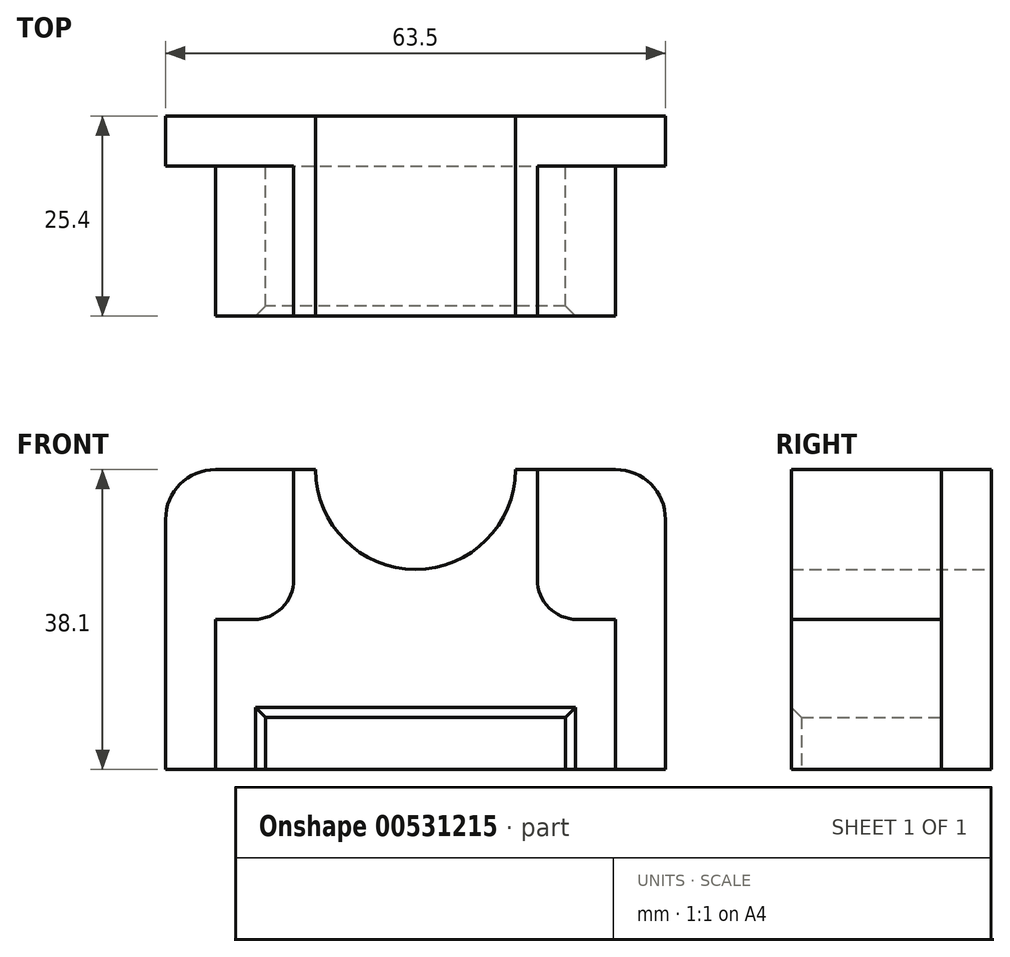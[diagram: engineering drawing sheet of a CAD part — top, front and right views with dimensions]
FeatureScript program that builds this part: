
annotation { "Feature Type Name" : "Feature", "Feature Type Description" : "" }
export const myFeature = defineFeature(function(context is Context, id is Id, definition is map)
    precondition{}
    {
        {
            var Q0;
            Q0=qCreatedBy(makeId("Front.planeOp"),FACE);
            var sketch = newSketch(context, id + "F0", { "sketchPlane" : qUnion([Q0])});
            skLineSegment(sketch, "E0.bottom", {"start": v(-25.4, 19.05) * mm, "end": v(-12.7, 19.05) * mm});
            skLineSegment(sketch, "E0.top", {"start": v(-31.75, -19.05) * mm, "end": v(31.75, -19.05) * mm});
            skLineSegment(sketch, "E0.left", {"start": v(-31.75, 12.7) * mm, "end": v(-31.75, -19.05) * mm});
            skLineSegment(sketch, "E0.right", {"start": v(31.75, 12.7) * mm, "end": v(31.75, -19.05) * mm});
            skPoint(sketch, "E0.middle", {"position": v(0, 0) * mm});
            skPoint(sketch, "E1.visualSharp", {"position": v(31.75, 19.05) * mm});
            skArc(sketch, "E1.filletArc", {"start": v(31.75, 12.7) * mm, "mid": v(29.9, 17.2) * mm, "end": v(25.4, 19.05) * mm});
            skPoint(sketch, "E2.visualSharp", {"position": v(-31.75, 19.05) * mm});
            skArc(sketch, "E2.filletArc", {"start": v(-25.4, 19.05) * mm, "mid": v(-29.9, 17.2) * mm, "end": v(-31.75, 12.7) * mm});
            skArc(sketch, "E3", {"start": v(-12.7, 19.05) * mm, "mid": v(0, 6.35) * mm, "end": v(12.7, 19.05) * mm});
            skLineSegment(sketch, "E4.trimOffspring", {"start": v(12.7, 19.05) * mm, "end": v(25.4, 19.05) * mm});
            skSolve(sketch);
        }
        {
            var Q0;
            Q0=makeQuery(id+"F0.imprint","IMPRINT",FACE,{"disambiguationData":[TD([[makeQuery(id+"F0.imprint","IMPRINT",EDGE,{"derivedFrom":sQuery(id+"F0.wireOp",EDGE,"E0.bottom")}),-1.0]])]});
            extrude(context, id + "F1", {"entities" : qUnion([Q0]), "depth" : 6.35 * mm, "offsetDistance" : 25.4 * mm});
        }
        {
            var Q0;
            Q0=makeQuery(id+"F1.opExtrude","CAP_FACE",FACE,{"disambiguationData":[OSD([sQuery(id+"F0.wireOp",EDGE,"E0.bottom"),sQuery(id+"F0.wireOp",EDGE,"E0.top"),sQuery(id+"F0.wireOp",EDGE,"E0.left"),sQuery(id+"F0.wireOp",EDGE,"E0.right"),sQuery(id+"F0.wireOp",EDGE,"E1.filletArc"),sQuery(id+"F0.wireOp",EDGE,"E2.filletArc"),sQuery(id+"F0.wireOp",EDGE,"E3"),sQuery(id+"F0.wireOp",EDGE,"E4.trimOffspring")])],"isStart":false});
            var sketch = newSketch(context, id + "F2", { "sketchPlane" : qUnion([Q0])});
            skLineSegment(sketch, "E5", {"start": v(-12.7, 19.05) * mm, "end": v(-15.47, 19.05) * mm});
            skLineSegment(sketch, "E6", {"start": v(-19.05, -19.05) * mm, "end": v(-25.4, -19.05) * mm});
            skLineSegment(sketch, "E7", {"start": v(19.05, -19.05) * mm, "end": v(25.4, -19.05) * mm});
            skLineSegment(sketch, "E8", {"start": v(-25.4, -19.05) * mm, "end": v(-25.4, 0) * mm});
            skLineSegment(sketch, "E9", {"start": v(25.4, -19.05) * mm, "end": v(25.4, 0) * mm});
            skLineSegment(sketch, "E10", {"start": v(25.4, -19.05) * mm, "end": v(19.05, -19.05) * mm});
            skLineSegment(sketch, "E11", {"start": v(-25.4, -19.05) * mm, "end": v(-19.05, -19.05) * mm});
            skArc(sketch, "E12", {"start": v(-12.7, 19.05) * mm, "mid": v(0, 6.35) * mm, "end": v(12.7, 19.05) * mm});
            skLineSegment(sketch, "E13", {"start": v(-15.47, 19.05) * mm, "end": v(-15.47, 0) * mm});
            skLineSegment(sketch, "E14", {"start": v(-15.47, 0) * mm, "end": v(-25.4, 0) * mm});
            skLineSegment(sketch, "E15", {"start": v(12.7, 19.05) * mm, "end": v(15.47, 19.05) * mm});
            skLineSegment(sketch, "E16", {"start": v(15.47, 19.05) * mm, "end": v(15.47, 0) * mm});
            skLineSegment(sketch, "E17", {"start": v(15.47, 0) * mm, "end": v(25.4, 0) * mm});
            skLineSegment(sketch, "E18", {"start": v(-19.05, -19.05) * mm, "end": v(-19.05, -12.42) * mm});
            skLineSegment(sketch, "E19", {"start": v(-19.05, -12.42) * mm, "end": v(19.05, -12.42) * mm});
            skLineSegment(sketch, "E20", {"start": v(19.05, -19.05) * mm, "end": v(19.05, -12.42) * mm});
            skPoint(sketch, "E21.orphan", {"position": v(0, -19.05) * mm});
            skSolve(sketch);
        }
        {
            var Q0;
            Q0=makeQuery(id+"F2.imprint","IMPRINT",FACE,{"disambiguationData":[TD([[makeQuery(id+"F2.imprint","IMPRINT",EDGE,{"derivedFrom":sQuery(id+"F2.wireOp",EDGE,"E5")}),-1.0]])]});
            extrude(context, id + "F3", {"entities" : qUnion([Q0]), "operationType" : NewBodyOperationType.ADD, "depth" : 19.05 * mm, "offsetDistance" : 25.4 * mm});
        }
        {
            var Q0;
            Q0=makeQuery(id+"F3.opExtrude","SWEPT_EDGE",EDGE,{"disambiguationData":[OSD([sQuery(id+"F2.wireOp",EDGE,"E13"),sQuery(id+"F2.wireOp",EDGE,"E14")])]});
            var Q1;
            Q1=makeQuery(id+"F3.opExtrude","SWEPT_EDGE",EDGE,{"disambiguationData":[OSD([sQuery(id+"F2.wireOp",EDGE,"E16"),sQuery(id+"F2.wireOp",EDGE,"E17")])]});
            fillet(context, id + "F4", {"entities" : qUnion([Q0, Q1]), "radius" : 5.08 * mm, "tangentPropagation" : true, "allowEdgeOverflow" : false});
        }
        {
            var Q0;
            Q0=makeQuery(id+"F3.opExtrude","CAP_EDGE",EDGE,{"disambiguationData":[OSD([sQuery(id+"F2.wireOp",EDGE,"E19")])],"isStart":false});
            var Q1;
            Q1=makeQuery(id+"F3.opExtrude","CAP_EDGE",EDGE,{"disambiguationData":[OSD([sQuery(id+"F2.wireOp",EDGE,"E18")])],"isStart":false});
            var Q2;
            Q2=makeQuery(id+"F3.opExtrude","CAP_EDGE",EDGE,{"disambiguationData":[OSD([sQuery(id+"F2.wireOp",EDGE,"E20")])],"isStart":false});
            chamfer(context, id + "F5", {"entities" : qUnion([Q0, Q1, Q2]), "width" : 1.27 * mm, "tangentPropagation" : true});
        }
    });
